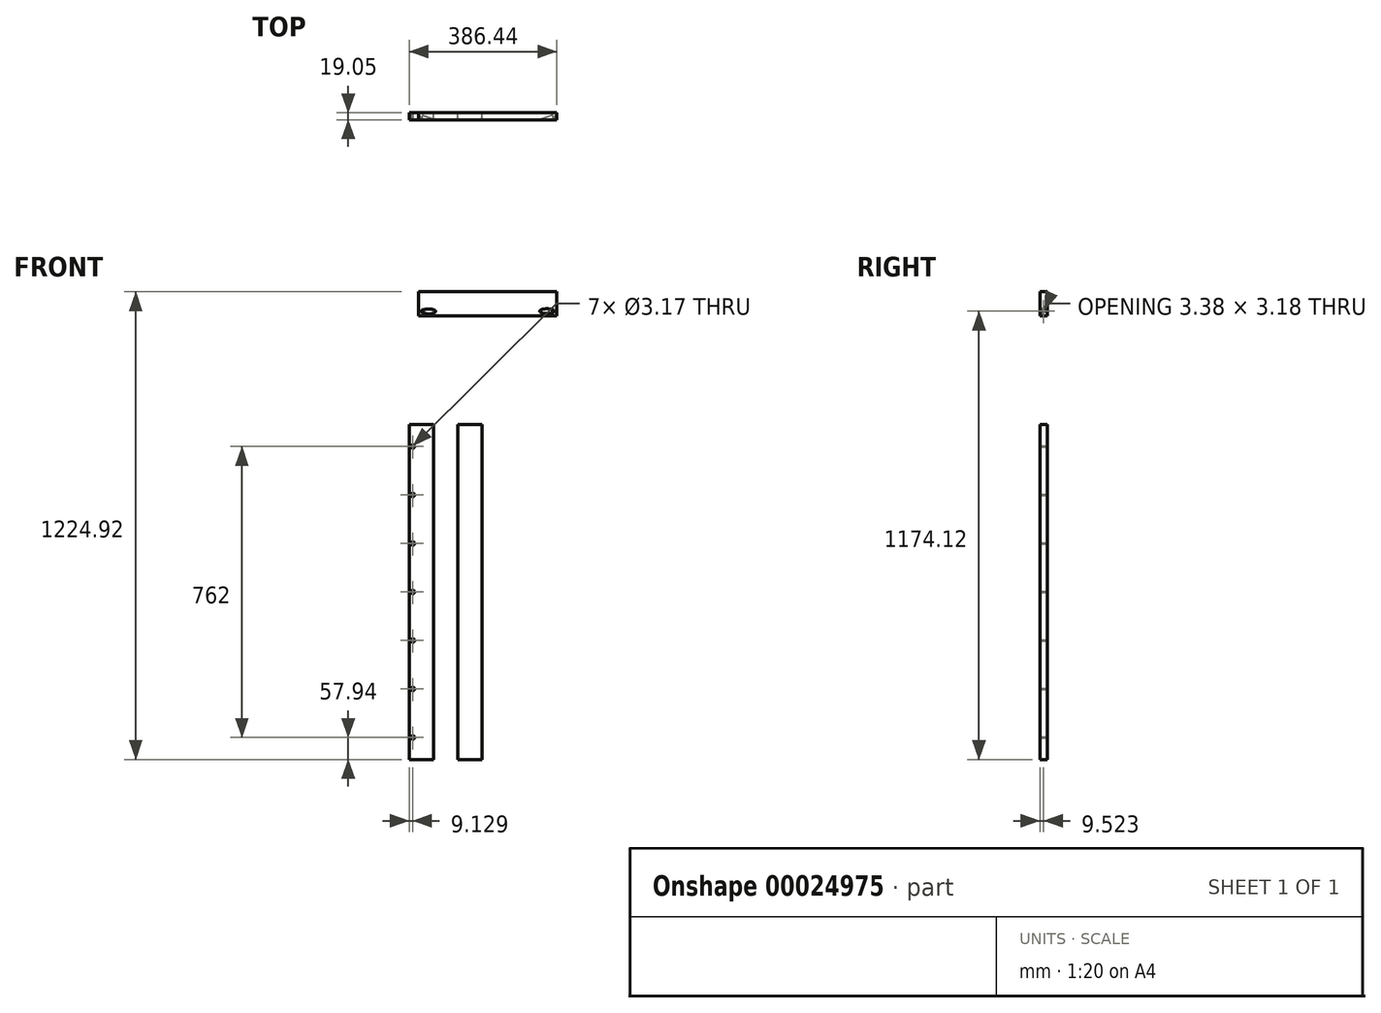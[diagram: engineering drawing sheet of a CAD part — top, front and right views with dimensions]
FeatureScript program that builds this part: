
annotation { "Feature Type Name" : "Feature", "Feature Type Description" : "" }
export const myFeature = defineFeature(function(context is Context, id is Id, definition is map)
    precondition{}
    {
        {
            var Q0;
            Q0=qCreatedBy(makeId("Front.planeOp"),FACE);
            var sketch = newSketch(context, id + "F0", { "sketchPlane" : qUnion([Q0])});
            skLineSegment(sketch, "E0.bottom", {"start": v(-574.17, 295.8) * mm, "end": v(-510.67, 295.8) * mm});
            skLineSegment(sketch, "E0.top", {"start": v(-574.17, -582.08) * mm, "end": v(-510.67, -582.08) * mm});
            skLineSegment(sketch, "E0.left", {"start": v(-574.17, 295.8) * mm, "end": v(-574.17, -582.08) * mm});
            skLineSegment(sketch, "E0.right", {"start": v(-510.67, 295.8) * mm, "end": v(-510.67, -582.08) * mm});
            skLineSegment(sketch, "E1.bottom", {"start": v(-549.68, 642.84) * mm, "end": v(-187.73, 642.84) * mm});
            skLineSegment(sketch, "E1.top", {"start": v(-549.68, 579.34) * mm, "end": v(-187.73, 579.34) * mm});
            skLineSegment(sketch, "E1.left", {"start": v(-549.68, 642.84) * mm, "end": v(-549.68, 579.34) * mm});
            skLineSegment(sketch, "E1.right", {"start": v(-187.73, 642.84) * mm, "end": v(-187.73, 579.34) * mm});
            skSolve(sketch);
        }
        {
            var Q0;
            Q0 = qSketchRegion(id + "F0", true);
            extrude(context, id + "F1", {"entities" : qUnion([Q0]), "depth" : 19.05 * mm});
        }
        {
            var Q0;
            Q0=makeQuery(id+"F1.opExtrude","SWEPT_FACE",FACE,{"disambiguationData":[OSD([sQuery(id+"F0.wireOp",EDGE,"E1.left")])]});
            var sketch = newSketch(context, id + "F2", { "sketchPlane" : qUnion([Q0])});
            skLineSegment(sketch, "E2", {"start": v(9.53, 642.84) * mm, "end": v(9.53, 579.34) * mm});
            skSolve(sketch);
        }
        {
            var Q0;
            Q0=makeQuery(id+"F1.opExtrude","CAP_EDGE",EDGE,{"disambiguationData":[OSD([sQuery(id+"F0.wireOp",EDGE,"E1.left")])],"isStart":true});
            cPlane(context, id + "F3", {"entities" : qUnion([Q0]), "cplaneType" : CPlaneType.LINE_ANGLE, "offset" : 152.4 * mm, "angle" : 20 * degree, "width" : 152.4 * mm, "height" : 152.4 * mm});
        }
        {
            var Q0;
            Q0=qCreatedBy(id+"F3.planeOp",FACE);
            var sketch = newSketch(context, id + "F4", { "sketchPlane" : qUnion([Q0])});
            skPoint(sketch, "E3", {"position": v(196.95, 592.04) * mm});
            skSolve(sketch);
        }
        {
            var Q0;
            Q0=sQuery(id+"F4.wireOp",VERTEX,"E3");
            var Q1;
            Q1=makeQuery(id+"F1.opExtrude","SWEPT_BODY",BODY,{"disambiguationData":[OSD([sQuery(id+"F0.wireOp",EDGE,"E1.bottom"),sQuery(id+"F0.wireOp",EDGE,"E1.top"),sQuery(id+"F0.wireOp",EDGE,"E1.left"),sQuery(id+"F0.wireOp",EDGE,"E1.right")])]});
            hole(context, id + "F5", {"style" : HoleStyle.SIMPLE, "endStyle" : HoleEndStyle.THROUGH, "holeDiameter" : 3.17 * mm, "locations" : qUnion([Q0]), "scope" : qUnion([Q1]), "isTappedThrough" : true, "startStyle" : HoleStartStyle.PART});
        }
        {
            var Q0;
            Q0=qCreatedBy(id+"F3.planeOp",FACE);
            cPlane(context, id + "F6", {"entities" : qUnion([Q0]), "cplaneType" : CPlaneType.OFFSET, "offset" : 12.7 * mm, "oppositeDirection" : true, "width" : 152.4 * mm, "height" : 152.4 * mm});
        }
        {
            var Q0;
            Q0=qCreatedBy(id+"F6.planeOp",FACE);
            var sketch = newSketch(context, id + "F7", { "sketchPlane" : qUnion([Q0])});
            skPoint(sketch, "E4", {"position": v(196.95, 591.46) * mm});
            skSolve(sketch);
        }
        {
            var Q0;
            Q0=sQuery(id+"F7.wireOp",VERTEX,"E4");
            var Q1;
            Q1=makeQuery(id+"F1.opExtrude","SWEPT_BODY",BODY,{"disambiguationData":[OSD([sQuery(id+"F0.wireOp",EDGE,"E1.bottom"),sQuery(id+"F0.wireOp",EDGE,"E1.top"),sQuery(id+"F0.wireOp",EDGE,"E1.left"),sQuery(id+"F0.wireOp",EDGE,"E1.right")])]});
            hole(context, id + "F8", {"style" : HoleStyle.SIMPLE, "endStyle" : HoleEndStyle.THROUGH, "holeDiameter" : 12.7 * mm, "locations" : qUnion([Q0]), "scope" : qUnion([Q1]), "isTappedThrough" : true, "startStyle" : HoleStartStyle.PART});
        }
        {
            var Q0;
            Q0=makeQuery(id+"F1.opExtrude","CAP_EDGE",EDGE,{"disambiguationData":[OSD([sQuery(id+"F0.wireOp",EDGE,"E1.right")])],"isStart":true});
            cPlane(context, id + "F9", {"entities" : qUnion([Q0]), "cplaneType" : CPlaneType.LINE_ANGLE, "offset" : 152.4 * mm, "angle" : 340 * degree, "width" : 152.4 * mm, "height" : 152.4 * mm});
        }
        {
            var Q0;
            Q0=qCreatedBy(id+"F9.planeOp",FACE);
            var sketch = newSketch(context, id + "F10", { "sketchPlane" : qUnion([Q0])});
            skPoint(sketch, "E5", {"position": v(-55.26, 592.04) * mm});
            skSolve(sketch);
        }
        {
            var Q0;
            Q0=sQuery(id+"F10.wireOp",VERTEX,"E5");
            var Q1;
            Q1=makeQuery(id+"F1.opExtrude","SWEPT_BODY",BODY,{"disambiguationData":[OSD([sQuery(id+"F0.wireOp",EDGE,"E1.bottom"),sQuery(id+"F0.wireOp",EDGE,"E1.top"),sQuery(id+"F0.wireOp",EDGE,"E1.left"),sQuery(id+"F0.wireOp",EDGE,"E1.right")])]});
            hole(context, id + "F11", {"style" : HoleStyle.SIMPLE, "endStyle" : HoleEndStyle.THROUGH, "oppositeDirection" : true, "holeDiameter" : 3.17 * mm, "locations" : qUnion([Q0]), "scope" : qUnion([Q1]), "isTappedThrough" : true, "startStyle" : HoleStartStyle.PART});
        }
        {
            var Q0;
            Q0=qCreatedBy(id+"F9.planeOp",FACE);
            cPlane(context, id + "F12", {"entities" : qUnion([Q0]), "cplaneType" : CPlaneType.OFFSET, "offset" : 12.7 * mm, "width" : 152.4 * mm, "height" : 152.4 * mm});
        }
        {
            var Q0;
            Q0=qCreatedBy(id+"F12.planeOp",FACE);
            var sketch = newSketch(context, id + "F13", { "sketchPlane" : qUnion([Q0])});
            skPoint(sketch, "E6", {"position": v(-55.26, 592.04) * mm});
            skSolve(sketch);
        }
        {
            var Q0;
            Q0=sQuery(id+"F13.wireOp",VERTEX,"E6");
            var Q1;
            Q1=makeQuery(id+"F1.opExtrude","SWEPT_BODY",BODY,{"disambiguationData":[OSD([sQuery(id+"F0.wireOp",EDGE,"E1.bottom"),sQuery(id+"F0.wireOp",EDGE,"E1.top"),sQuery(id+"F0.wireOp",EDGE,"E1.left"),sQuery(id+"F0.wireOp",EDGE,"E1.right")])]});
            hole(context, id + "F14", {"style" : HoleStyle.SIMPLE, "endStyle" : HoleEndStyle.THROUGH, "oppositeDirection" : true, "holeDiameter" : 12.7 * mm, "locations" : qUnion([Q0]), "scope" : qUnion([Q1]), "isTappedThrough" : true, "startStyle" : HoleStartStyle.PART});
        }
        {
            var Q0;
            Q0=makeQuery(id+"F1.opExtrude","CAP_FACE",FACE,{"disambiguationData":[OSD([sQuery(id+"F0.wireOp",EDGE,"E0.bottom"),sQuery(id+"F0.wireOp",EDGE,"E0.top"),sQuery(id+"F0.wireOp",EDGE,"E0.left"),sQuery(id+"F0.wireOp",EDGE,"E0.right")])],"isStart":false});
            var sketch = newSketch(context, id + "F15", { "sketchPlane" : qUnion([Q0])});
            skPoint(sketch, "E7", {"position": v(-574.17, 295.8) * mm});
            skPoint(sketch, "E8", {"position": v(-565.04, 295.8) * mm});
            skPoint(sketch, "E9", {"position": v(-565.04, -143.14) * mm});
            skPoint(sketch, "E9.positionSnap0", {"position": v(-574.17, -143.14) * mm});
            skPoint(sketch, "E10", {"position": v(-565.04, -524.14) * mm});
            skPoint(sketch, "E11.0.1.0", {"position": v(-565.04, -397.14) * mm});
            skPoint(sketch, "E11.0.2.0", {"position": v(-565.04, -270.14) * mm});
            skPoint(sketch, "E11.0.4.0", {"position": v(-565.04, -16.14) * mm});
            skPoint(sketch, "E11.0.5.0", {"position": v(-565.04, 110.86) * mm});
            skPoint(sketch, "E11.0.6.0", {"position": v(-565.04, 237.86) * mm});
            skLineSegment(sketch, "E11.direction1", {"start": v(-883.51, -524.14) * mm, "end": v(-565.04, -524.14) * mm, "construction": true});
            skLineSegment(sketch, "E11.direction2", {"start": v(-565.04, -524.14) * mm, "end": v(-565.04, -397.14) * mm, "construction": true});
            skSolve(sketch);
        }
        {
            var Q0;
            Q0=sQuery(id+"F15.wireOp",VERTEX,"E10");
            var Q1;
            Q1=sQuery(id+"F15.wireOp",VERTEX,"E11.0.1.0");
            var Q2;
            Q2=sQuery(id+"F15.wireOp",VERTEX,"E11.0.2.0");
            var Q3;
            Q3=sQuery(id+"F15.wireOp",VERTEX,"E9");
            var Q4;
            Q4=sQuery(id+"F15.wireOp",VERTEX,"E11.0.4.0");
            var Q5;
            Q5=sQuery(id+"F15.wireOp",VERTEX,"E11.0.5.0");
            var Q6;
            Q6=sQuery(id+"F15.wireOp",VERTEX,"E11.0.6.0");
            var Q7;
            Q7=makeQuery(id+"F1.opExtrude","SWEPT_BODY",BODY,{"disambiguationData":[OSD([sQuery(id+"F0.wireOp",EDGE,"E0.bottom"),sQuery(id+"F0.wireOp",EDGE,"E0.top"),sQuery(id+"F0.wireOp",EDGE,"E0.left"),sQuery(id+"F0.wireOp",EDGE,"E0.right")])]});
            hole(context, id + "F16", {"style" : HoleStyle.C_SINK, "endStyle" : HoleEndStyle.THROUGH, "holeDiameter" : 3.17 * mm, "cSinkDiameter" : 9.52 * mm, "cSinkAngle" : 90 * degree, "locations" : qUnion([Q0, Q1, Q2, Q3, Q4, Q5, Q6]), "scope" : qUnion([Q7]), "isTappedThrough" : true, "startStyle" : HoleStartStyle.PART});
        }
        {
            var Q0;
            Q0=makeQuery(id+"F1.opExtrude","SWEPT_BODY",BODY,{"disambiguationData":[OSD([sQuery(id+"F0.wireOp",EDGE,"E0.bottom"),sQuery(id+"F0.wireOp",EDGE,"E0.top"),sQuery(id+"F0.wireOp",EDGE,"E0.left"),sQuery(id+"F0.wireOp",EDGE,"E0.right")])]});
            transform(context, id + "F17", {"entities" : qUnion([Q0]), "transformType" : TransformType.TRANSLATION_3D, "dx" : 152.4 * mm, "dy" : 0 * mm, "dz" : 0 * mm, "makeCopy" : true});
        }
        {
            var Q0;
            Q0=makeQuery(id+"F17.opPattern","COPY",BODY,{"derivedFrom":makeQuery(id+"F1.opExtrude","SWEPT_BODY",BODY,{"disambiguationData":[OSD([sQuery(id+"F0.wireOp",EDGE,"E0.bottom"),sQuery(id+"F0.wireOp",EDGE,"E0.top"),sQuery(id+"F0.wireOp",EDGE,"E0.left"),sQuery(id+"F0.wireOp",EDGE,"E0.right")])]}),"instanceName":"1"});
            deleteBodies(context, id + "F18", {"entities" : qUnion([Q0])});
        }
        {
            var Q0;
            Q0 = qSketchRegion(id + "F0", true);
            extrude(context, id + "F19", {"entities" : qUnion([Q0]), "depth" : 19.05 * mm});
        }
        {
            var Q0;
            Q0=makeQuery(id+"F19.opExtrude","SWEPT_BODY",BODY,{"disambiguationData":[OSD([sQuery(id+"F0.wireOp",EDGE,"E1.bottom"),sQuery(id+"F0.wireOp",EDGE,"E1.top"),sQuery(id+"F0.wireOp",EDGE,"E1.left"),sQuery(id+"F0.wireOp",EDGE,"E1.right")])]});
            transform(context, id + "F20", {"entities" : qUnion([Q0]), "transformType" : TransformType.TRANSLATION_3D, "dx" : 152.4 * mm, "dy" : 0 * mm, "dz" : 0 * mm, "makeCopy" : false});
        }
        {
            var Q0;
            Q0=makeQuery(id+"F19.opExtrude","SWEPT_BODY",BODY,{"disambiguationData":[OSD([sQuery(id+"F0.wireOp",EDGE,"E1.bottom"),sQuery(id+"F0.wireOp",EDGE,"E1.top"),sQuery(id+"F0.wireOp",EDGE,"E1.left"),sQuery(id+"F0.wireOp",EDGE,"E1.right")])]});
            deleteBodies(context, id + "F21", {"entities" : qUnion([Q0])});
        }
        {
            var Q0;
            Q0=makeQuery(id+"F19.opExtrude","SWEPT_BODY",BODY,{"disambiguationData":[OSD([sQuery(id+"F0.wireOp",EDGE,"E0.bottom"),sQuery(id+"F0.wireOp",EDGE,"E0.top"),sQuery(id+"F0.wireOp",EDGE,"E0.left"),sQuery(id+"F0.wireOp",EDGE,"E0.right")])]});
            transform(context, id + "F22", {"entities" : qUnion([Q0]), "transformType" : TransformType.TRANSLATION_3D, "dx" : 127 * mm, "dy" : 0 * mm, "dz" : 0 * mm, "makeCopy" : false});
        }
    });
